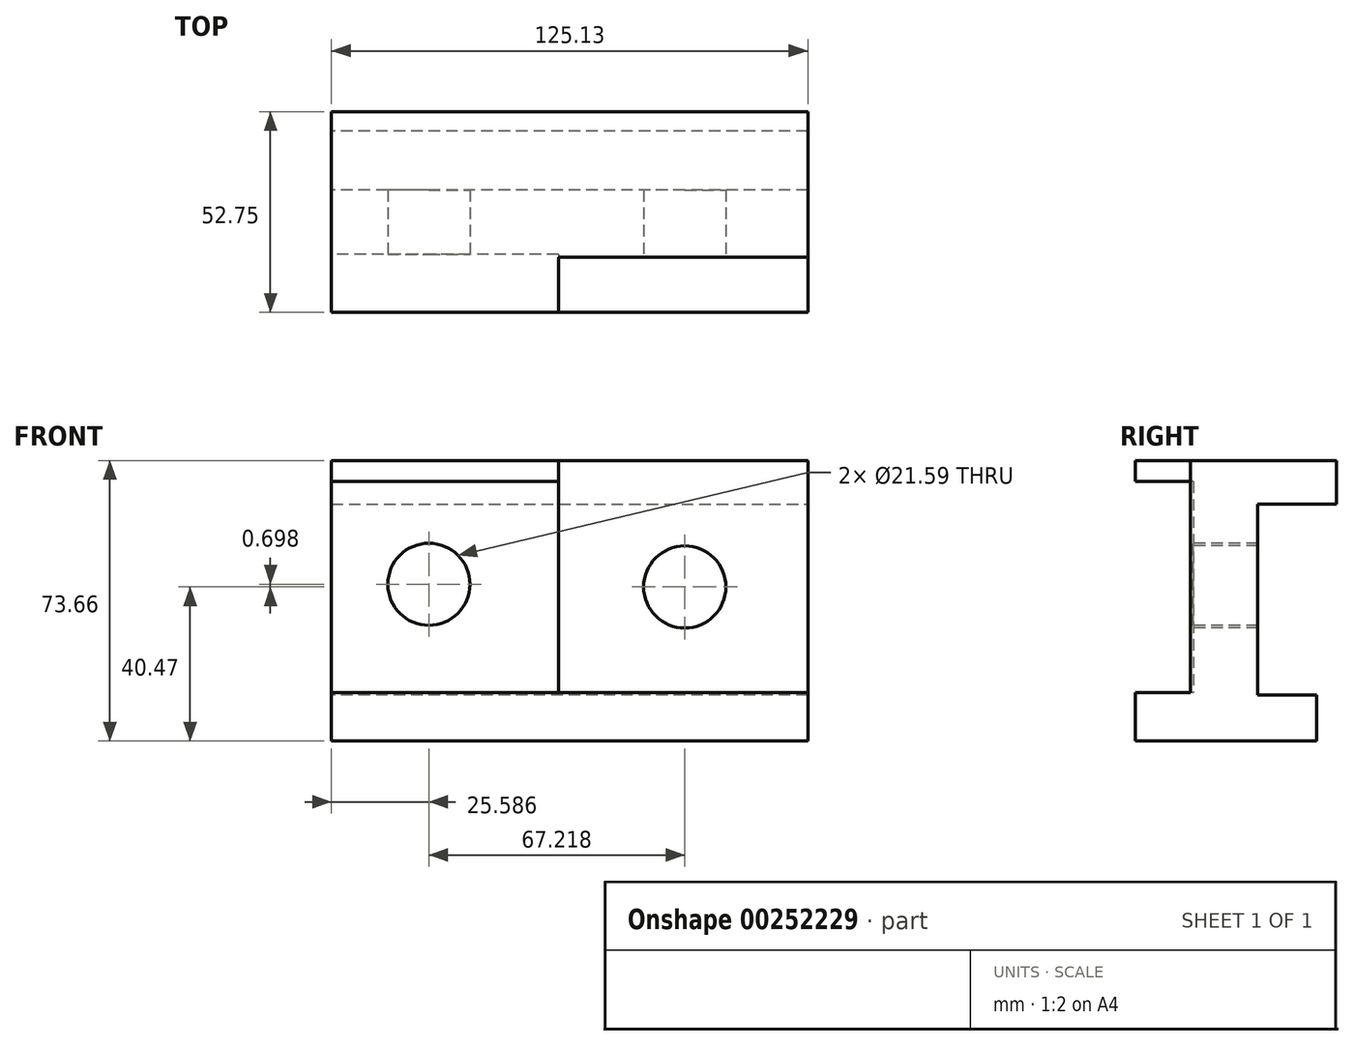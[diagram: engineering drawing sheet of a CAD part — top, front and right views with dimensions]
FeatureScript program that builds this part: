
annotation { "Feature Type Name" : "Feature", "Feature Type Description" : "" }
export const myFeature = defineFeature(function(context is Context, id is Id, definition is map)
    precondition{}
    {
        {
            var Q0;
            Q0=qCreatedBy(makeId("Top.planeOp"),FACE);
            var sketch = newSketch(context, id + "F0", { "sketchPlane" : qUnion([Q0])});
            skLineSegment(sketch, "E0.bottom", {"start": v(-59.66, 28.14) * mm, "end": v(65.47, 28.14) * mm});
            skLineSegment(sketch, "E0.top", {"start": v(-59.66, -39.54) * mm, "end": v(65.47, -39.54) * mm});
            skLineSegment(sketch, "E0.left", {"start": v(-59.66, 28.14) * mm, "end": v(-59.66, -39.54) * mm});
            skLineSegment(sketch, "E0.right", {"start": v(65.47, 28.14) * mm, "end": v(65.47, -39.54) * mm});
            skSolve(sketch);
        }
        {
            var Q0;
            Q0=makeQuery(id+"F0.imprint","IMPRINT",FACE,{"disambiguationData":[TD([[makeQuery(id+"F0.imprint","IMPRINT",EDGE,{"derivedFrom":sQuery(id+"F0.wireOp",EDGE,"E0.bottom")}),-1.0]])]});
            extrude(context, id + "F1", {"entities" : qUnion([Q0]), "depth" : 12.7 * mm});
        }
        {
            var Q0;
            Q0=makeQuery(id+"F1.opExtrude","CAP_FACE",FACE,{"disambiguationData":[OSD([sQuery(id+"F0.wireOp",EDGE,"E0.bottom"),sQuery(id+"F0.wireOp",EDGE,"E0.top"),sQuery(id+"F0.wireOp",EDGE,"E0.left"),sQuery(id+"F0.wireOp",EDGE,"E0.right")])],"isStart":false});
            var sketch = newSketch(context, id + "F2", { "sketchPlane" : qUnion([Q0])});
            skLineSegment(sketch, "E1.bottom", {"start": v(-59.66, 28.14) * mm, "end": v(65.47, 28.14) * mm});
            skLineSegment(sketch, "E1.top", {"start": v(-59.66, -39.54) * mm, "end": v(65.47, -39.54) * mm});
            skLineSegment(sketch, "E1.left", {"start": v(-59.66, 28.14) * mm, "end": v(-59.66, -39.54) * mm});
            skLineSegment(sketch, "E1.right", {"start": v(65.47, 28.14) * mm, "end": v(65.47, -39.54) * mm});
            skSolve(sketch);
        }
        {
            var Q0;
            Q0=makeQuery(id+"F2.imprint","IMPRINT",FACE,{"disambiguationData":[TD([[makeQuery(id+"F2.imprint","IMPRINT",EDGE,{"derivedFrom":sQuery(id+"F2.wireOp",EDGE,"E1.bottom")}),-1.0]])]});
            extrude(context, id + "F3", {"entities" : qUnion([Q0]), "operationType" : NewBodyOperationType.ADD, "depth" : 60.96 * mm});
        }
        {
            var Q0;
            Q0=makeQuery(id+"F3.opExtrude","CAP_FACE",FACE,{"disambiguationData":[OSD([sQuery(id+"F2.wireOp",EDGE,"E1.bottom"),sQuery(id+"F2.wireOp",EDGE,"E1.top"),sQuery(id+"F2.wireOp",EDGE,"E1.left"),sQuery(id+"F2.wireOp",EDGE,"E1.right")])],"isStart":false});
            var sketch = newSketch(context, id + "F4", { "sketchPlane" : qUnion([Q0])});
            skPoint(sketch, "E2.firstSnap0", {"position": v(2.9, -39.54) * mm});
            skLineSegment(sketch, "E2.bottom", {"start": v(0, -39.54) * mm, "end": v(65.47, -39.54) * mm});
            skLineSegment(sketch, "E2.top", {"start": v(0, -25.12) * mm, "end": v(65.47, -25.12) * mm});
            skLineSegment(sketch, "E2.left", {"start": v(0, -39.54) * mm, "end": v(0, -25.12) * mm});
            skLineSegment(sketch, "E2.right", {"start": v(65.47, -39.54) * mm, "end": v(65.47, -25.12) * mm});
            skSolve(sketch);
        }
        {
            var Q0;
            Q0=makeQuery(id+"F4.imprint","IMPRINT",FACE,{"disambiguationData":[TD([[makeQuery(id+"F4.imprint","IMPRINT",EDGE,{"derivedFrom":sQuery(id+"F4.wireOp",EDGE,"E2.bottom")}),1.0]])]});
            extrude(context, id + "F5", {"entities" : qUnion([Q0]), "operationType" : NewBodyOperationType.REMOVE, "oppositeDirection" : true, "depth" : 60.96 * mm});
        }
        {
            var Q0;
            Q0=makeQuery(id+"F3.boolean.opBoolean","MERGE",FACE,{"derivedFrom":[makeQuery(id+"F1.opExtrude","SWEPT_FACE",FACE,{"disambiguationData":[OSD([sQuery(id+"F0.wireOp",EDGE,"E0.top")])]}),makeQuery(id+"F3.opExtrude","SWEPT_FACE",FACE,{"disambiguationData":[OSD([sQuery(id+"F2.wireOp",EDGE,"E1.top")])]})]});
            var sketch = newSketch(context, id + "F6", { "sketchPlane" : qUnion([Q0])});
            skLineSegment(sketch, "E3.bottom", {"start": v(0, 12.7) * mm, "end": v(-59.66, 12.7) * mm});
            skLineSegment(sketch, "E3.top", {"start": v(0, 68.15) * mm, "end": v(-59.66, 68.15) * mm});
            skLineSegment(sketch, "E3.left", {"start": v(0, 12.7) * mm, "end": v(0, 68.15) * mm});
            skLineSegment(sketch, "E3.right", {"start": v(-59.66, 12.7) * mm, "end": v(-59.66, 68.15) * mm});
            skSolve(sketch);
        }
        {
            var Q0;
            Q0=makeQuery(id+"F6.imprint","IMPRINT",FACE,{"disambiguationData":[TD([[makeQuery(id+"F6.imprint","IMPRINT",EDGE,{"derivedFrom":sQuery(id+"F6.wireOp",EDGE,"E3.bottom")}),-1.0]])]});
            extrude(context, id + "F7", {"entities" : qUnion([Q0]), "operationType" : NewBodyOperationType.REMOVE, "oppositeDirection" : true, "depth" : 10.16 * mm});
        }
        {
            var Q0;
            Q0=makeQuery(id+"F5.boolean.opBoolean","COPY",FACE,{"derivedFrom":makeQuery(id+"F5.opExtrude","SWEPT_FACE",FACE,{"disambiguationData":[OSD([sQuery(id+"F4.wireOp",EDGE,"E2.top")])]})});
            extrude(context, id + "F8", {"entities" : qUnion([Q0]), "operationType" : NewBodyOperationType.ADD, "depth" : 5.08 * mm});
        }
        {
            var Q0;
            Q0=makeQuery(id+"F8.opExtrude","CAP_FACE",FACE,{"disambiguationData":[OSD([sQuery(id+"F4.wireOp",EDGE,"E2.top")])],"isStart":false});
            var Q1;
            Q1=makeQuery(id+"F7.boolean.opBoolean","COPY",FACE,{"derivedFrom":makeQuery(id+"F7.opExtrude","CAP_FACE",FACE,{"disambiguationData":[OSD([sQuery(id+"F6.wireOp",EDGE,"E3.bottom"),sQuery(id+"F6.wireOp",EDGE,"E3.top"),sQuery(id+"F6.wireOp",EDGE,"E3.left"),sQuery(id+"F6.wireOp",EDGE,"E3.right")])],"isStart":false})});
            extrude(context, id + "F9", {"entities" : qUnion([Q0, Q1]), "operationType" : NewBodyOperationType.REMOVE, "oppositeDirection" : true, "depth" : 5.08 * mm});
        }
        {
            var Q0;
            Q0=makeQuery(id+"F3.boolean.opBoolean","MERGE",FACE,{"derivedFrom":[makeQuery(id+"F1.opExtrude","SWEPT_FACE",FACE,{"disambiguationData":[OSD([sQuery(id+"F0.wireOp",EDGE,"E0.bottom")])]}),makeQuery(id+"F3.opExtrude","SWEPT_FACE",FACE,{"disambiguationData":[OSD([sQuery(id+"F2.wireOp",EDGE,"E1.bottom")])]})]});
            var sketch = newSketch(context, id + "F10", { "sketchPlane" : qUnion([Q0])});
            skLineSegment(sketch, "E4.bottom", {"start": v(-65.47, 62.25) * mm, "end": v(59.66, 62.25) * mm});
            skLineSegment(sketch, "E4.top", {"start": v(-65.47, 12) * mm, "end": v(59.66, 12) * mm});
            skLineSegment(sketch, "E4.left", {"start": v(-65.47, 62.25) * mm, "end": v(-65.47, 12) * mm});
            skLineSegment(sketch, "E4.right", {"start": v(59.66, 62.25) * mm, "end": v(59.66, 12) * mm});
            skSolve(sketch);
        }
        {
            var Q0;
            Q0=makeQuery(id+"F10.imprint","IMPRINT",FACE,{"disambiguationData":[TD([[makeQuery(id+"F10.imprint","IMPRINT",EDGE,{"derivedFrom":sQuery(id+"F10.wireOp",EDGE,"E4.bottom")}),-1.0]])]});
            extrude(context, id + "F11", {"entities" : qUnion([Q0]), "operationType" : NewBodyOperationType.REMOVE, "oppositeDirection" : true, "depth" : 35.56 * mm});
        }
        {
            var Q0;
            Q0=makeQuery(id+"F11.boolean.opBoolean","COPY",FACE,{"derivedFrom":makeQuery(id+"F11.opExtrude","SWEPT_FACE",FACE,{"disambiguationData":[OSD([sQuery(id+"F10.wireOp",EDGE,"E4.top")])]})});
            var sketch = newSketch(context, id + "F12", { "sketchPlane" : qUnion([Q0])});
            skLineSegment(sketch, "E5.bottom", {"start": v(65.47, 28.14) * mm, "end": v(-59.66, 28.14) * mm});
            skLineSegment(sketch, "E5.top", {"start": v(65.47, 8.03) * mm, "end": v(-59.66, 8.03) * mm});
            skLineSegment(sketch, "E5.left", {"start": v(65.47, 28.14) * mm, "end": v(65.47, 8.03) * mm});
            skLineSegment(sketch, "E5.right", {"start": v(-59.66, 28.14) * mm, "end": v(-59.66, 8.03) * mm});
            skSolve(sketch);
        }
        {
            var Q0;
            Q0=makeQuery(id+"F12.imprint","IMPRINT",FACE,{"disambiguationData":[TD([[makeQuery(id+"F12.imprint","IMPRINT",EDGE,{"derivedFrom":sQuery(id+"F12.wireOp",EDGE,"E5.bottom")}),1.0]])]});
            extrude(context, id + "F13", {"entities" : qUnion([Q0]), "operationType" : NewBodyOperationType.REMOVE, "oppositeDirection" : true, "depth" : 25.4 * mm});
        }
        {
            var Q0;
            {var subQ0=sQuery(id+"F4.wireOp",EDGE,"E2.top");Q0=makeQuery(id+"F8.boolean.opBoolean","MERGE",FACE,{"derivedFrom":[makeQuery(id+"F3.opExtrude","CAP_FACE",FACE,{"disambiguationData":[OSD([sQuery(id+"F2.wireOp",EDGE,"E1.bottom"),sQuery(id+"F2.wireOp",EDGE,"E1.top"),sQuery(id+"F2.wireOp",EDGE,"E1.left"),sQuery(id+"F2.wireOp",EDGE,"E1.right")])],"isStart":false}),makeQuery(id+"F8.opExtrude","SWEPT_FACE",FACE,{"disambiguationData":[OSD([subQ0]),TDD([makeQuery(id+"F5.boolean.opBoolean","COPY",EDGE,{"derivedFrom":makeQuery(id+"F5.opExtrude","CAP_EDGE",EDGE,{"disambiguationData":[OSD([subQ0])],"isStart":true})})])]})]});}
            var sketch = newSketch(context, id + "F14", { "sketchPlane" : qUnion([Q0])});
            skLineSegment(sketch, "E6.bottom", {"start": v(65.47, 19.3) * mm, "end": v(-59.66, 19.3) * mm});
            skLineSegment(sketch, "E6.top", {"start": v(65.47, 28.14) * mm, "end": v(-59.66, 28.14) * mm});
            skLineSegment(sketch, "E6.left", {"start": v(65.47, 19.3) * mm, "end": v(65.47, 28.14) * mm});
            skLineSegment(sketch, "E6.right", {"start": v(-59.66, 19.3) * mm, "end": v(-59.66, 28.14) * mm});
            skSolve(sketch);
        }
        {
            var Q0;
            Q0=makeQuery(id+"F14.imprint","IMPRINT",FACE,{"disambiguationData":[TD([[makeQuery(id+"F14.imprint","IMPRINT",EDGE,{"derivedFrom":sQuery(id+"F14.wireOp",EDGE,"E6.bottom")}),-1.0]])]});
            extrude(context, id + "F15", {"entities" : qUnion([Q0]), "operationType" : NewBodyOperationType.REMOVE, "oppositeDirection" : true, "depth" : 25.4 * mm});
        }
        {
            var Q0;
            {var subQ0=sQuery(id+"F4.wireOp",EDGE,"E2.top");Q0=makeQuery(id+"F8.boolean.opBoolean","MERGE",FACE,{"derivedFrom":[makeQuery(id+"F3.opExtrude","CAP_FACE",FACE,{"disambiguationData":[OSD([sQuery(id+"F2.wireOp",EDGE,"E1.bottom"),sQuery(id+"F2.wireOp",EDGE,"E1.top"),sQuery(id+"F2.wireOp",EDGE,"E1.left"),sQuery(id+"F2.wireOp",EDGE,"E1.right")])],"isStart":false}),makeQuery(id+"F8.opExtrude","SWEPT_FACE",FACE,{"disambiguationData":[OSD([subQ0]),TDD([makeQuery(id+"F5.boolean.opBoolean","COPY",EDGE,{"derivedFrom":makeQuery(id+"F5.opExtrude","CAP_EDGE",EDGE,{"disambiguationData":[OSD([subQ0])],"isStart":true})})])]})]});}
            var sketch = newSketch(context, id + "F16", { "sketchPlane" : qUnion([Q0])});
            skLineSegment(sketch, "E7.bottom", {"start": v(65.47, 13.2) * mm, "end": v(-59.66, 13.2) * mm});
            skLineSegment(sketch, "E7.top", {"start": v(65.47, 19.3) * mm, "end": v(-59.66, 19.3) * mm});
            skLineSegment(sketch, "E7.left", {"start": v(65.47, 13.2) * mm, "end": v(65.47, 19.3) * mm});
            skLineSegment(sketch, "E7.right", {"start": v(-59.66, 13.2) * mm, "end": v(-59.66, 19.3) * mm});
            skSolve(sketch);
        }
        {
            var Q0;
            Q0=makeQuery(id+"F16.imprint","IMPRINT",FACE,{"disambiguationData":[TD([[makeQuery(id+"F16.imprint","IMPRINT",EDGE,{"derivedFrom":sQuery(id+"F16.wireOp",EDGE,"E7.bottom")}),-1.0]])]});
            extrude(context, id + "F17", {"entities" : qUnion([Q0]), "operationType" : NewBodyOperationType.REMOVE, "oppositeDirection" : true, "depth" : 25.4 * mm});
        }
        {
            var Q0;
            Q0=makeQuery(id+"F9.boolean.opBoolean","COPY",FACE,{"derivedFrom":makeQuery(id+"F9.opExtrude","CAP_FACE",FACE,{"disambiguationData":[OSD([sQuery(id+"F6.wireOp",EDGE,"E3.bottom"),sQuery(id+"F6.wireOp",EDGE,"E3.top"),sQuery(id+"F6.wireOp",EDGE,"E3.left"),sQuery(id+"F6.wireOp",EDGE,"E3.right")])],"isStart":false})});
            var sketch = newSketch(context, id + "F18", { "sketchPlane" : qUnion([Q0])});
            skCircle(sketch, "E8", {"center": v(-34.07, 41.17) * mm, "radius": 10.28 * mm});
            skSolve(sketch);
        }
        {
            var Q0;
            Q0=sQuery(id+"F18.wireOp",VERTEX,"E8.center");
            var Q1;
            Q1=makeQuery(id+"F1.opExtrude","SWEPT_BODY",BODY,{"disambiguationData":[OSD([sQuery(id+"F0.wireOp",EDGE,"E0.bottom"),sQuery(id+"F0.wireOp",EDGE,"E0.top"),sQuery(id+"F0.wireOp",EDGE,"E0.left"),sQuery(id+"F0.wireOp",EDGE,"E0.right")])]});
            hole(context, id + "F19", {"style" : HoleStyle.SIMPLE, "endStyle" : HoleEndStyle.THROUGH, "holeDiameter" : 21.59 * mm, "tappedDepth" : 12.7 * mm, "tapClearance" : 3, "locations" : qUnion([Q0]), "scope" : qUnion([Q1])});
        }
        {
            var Q0;
            Q0=makeQuery(id+"F9.boolean.opBoolean","COPY",FACE,{"derivedFrom":makeQuery(id+"F9.opExtrude","CAP_FACE",FACE,{"disambiguationData":[OSD([sQuery(id+"F4.wireOp",EDGE,"E2.top")])],"isStart":false})});
            var sketch = newSketch(context, id + "F20", { "sketchPlane" : qUnion([Q0])});
            skCircle(sketch, "E9", {"center": v(33.14, 40.47) * mm, "radius": 10.56 * mm});
            skSolve(sketch);
        }
        {
            var Q0;
            Q0=sQuery(id+"F20.wireOp",VERTEX,"E9.center");
            var Q1;
            Q1=makeQuery(id+"F1.opExtrude","SWEPT_BODY",BODY,{"disambiguationData":[OSD([sQuery(id+"F0.wireOp",EDGE,"E0.bottom"),sQuery(id+"F0.wireOp",EDGE,"E0.top"),sQuery(id+"F0.wireOp",EDGE,"E0.left"),sQuery(id+"F0.wireOp",EDGE,"E0.right")])]});
            hole(context, id + "F21", {"style" : HoleStyle.SIMPLE, "endStyle" : HoleEndStyle.THROUGH, "holeDiameter" : 21.59 * mm, "tappedDepth" : 12.7 * mm, "tapClearance" : 3, "locations" : qUnion([Q0]), "scope" : qUnion([Q1])});
        }
    });
